# Revit family: P404
name_source: partatom
category: Generic Models
revit_build: Autodesk Revit Architecture 2012 (Build: 20110309_2315(x64)
units: mm (PartAtom-declared; Revit-internal decimal feet)

## types (1)
- P404
    CONNECTIVITY- Input Terminals- Analog = VGA 15-pin D-SUB, RCA Composite
    CONNECTIVITY- Input Terminals- Audio = 3.5mm Audio Mini Jack x2, DisplayPort Audio x2, HDMI Audio x3
    CONNECTIVITY- Input Terminals- Data = microSD (Media Player), USB 2.0 (Media Player), USB 2.0 (Service), USB Type-B (Upstream), USB 2.0 x2 (Compute Module, Powered 5V/2A)
    CONNECTIVITY- Input Terminals- Digital = HDMI 2.0 x2 (with HDCP), DVI-D (with HDCP), DisplayPort x2 (with HDCP)
    CONNECTIVITY- Input Terminals- External Control = LAN (100Mbit), 3.5 Mini Jack IR Remote, RS232C
    CONNECTIVITY- Output Terminals- Audio = 3.5mm Audio Mini Jack
    CONNECTIVITY- Output Terminals- Digital = DisplayPort (Outputs DisplayPort or OPS)
    CONNECTIVITY- Output Terminals- External Control = LAN (100mb)
    Description = 40-in. Professional Displays Ideal for Digital Signage Applications
    ENVIRONMENTAL CONDITIONS- Operating Altitude = 3000m (9843ft)
    ENVIRONMENTAL CONDITIONS- Operating Humidity = 20 - 80%
    ENVIRONMENTAL CONDITIONS- Operating Temperature = 0 to 40 C
    LCD MODULE- Aspect Ratio = 16 : 9
    LCD MODULE- Brightness (Typical/Minimum) = 550 cd/sqm / 700 cd/sqm
    LCD MODULE- Contras Ratio (Typical) = 4000:1
    LCD MODULE- Displayable Colors = Over 1.07 Billion
    LCD MODULE- Native Resolution = -
    LCD MODULE- Orientation = Landscape, Portrait, Face Up, Face Down
    LCD MODULE- Panel Haze = 25
    LCD MODULE- Panel Technology = SPVA
    LCD MODULE- Viewable Image Size = 40"
    LCD MODULE- Viewing Angle = 178deg Vert., 178deg Hor (89U/89D/89L/89R) @ CR>10
    Manufacturer = NEC Display Solutions
    Model = P404
    PHYSICAL SPECS- Bezel Width = 13.2mm / 12.2mm/ 13.2mm/ 13.2mm
    PHYSICAL SPECS- Net Dimensions (w/o Stand, WxHxD) = 36.1 x 20.9 x 2.2 in. (918.0 x 530.6 x 54.7 mm)
    PHYSICAL SPECS- Net Weight (w/o Stand) = 31.5 lbs / 14.3 kg
    PHYSICAL SPECS- Vesa Hole Configuration = 4x M6 x 12mm (300 x 300)
    POWER CONSUMPTION- Current Rating = 2.9A - 1.2A @ 100V - 240V
    POWER CONSUMPTION- Network Standby = 3W
    POWER CONSUMPTION- Normal Standby = < 0.5W
    POWER CONSUMPTION- On (Typ/Max) = 92W / 115W
    POWER CONSUMPTION- Speaker Rating = Integrated 10W x 10W, Optional 15W x 2
    SENSORS- Ambient Light Sensor = Integrated and programmable
    SENSORS- Human Sensor = Optional through KT-RC2 Accessory
    SENSORS- NFC Sensor = Integrated; works in conjunction with free NEC Intelligent Wireless Data Application
    SENSORS- Temperature Sensor = Integrated and programmable; linked to cooling fans
    URL = www.necdisplay.com

## geometry (parser evidence)
native form markers: Sweep x1
no freeform markers — native parametric forms only
